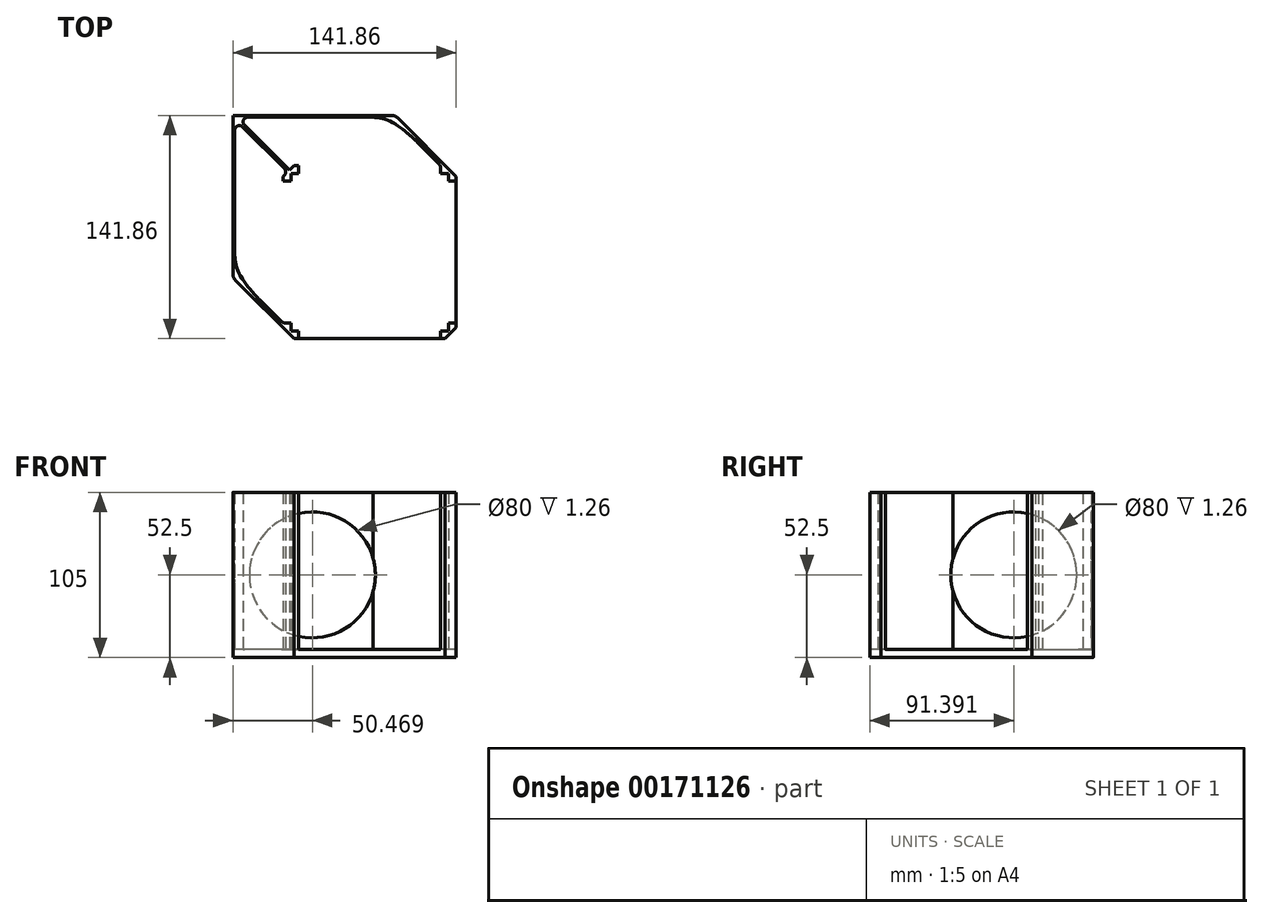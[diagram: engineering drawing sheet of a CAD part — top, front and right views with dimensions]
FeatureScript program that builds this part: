
annotation { "Feature Type Name" : "Feature", "Feature Type Description" : "" }
export const myFeature = defineFeature(function(context is Context, id is Id, definition is map)
    precondition{}
    {
        {
            var Q0;
            Q0=qCreatedBy(makeId("Top.planeOp"),FACE);
            var sketch = newSketch(context, id + "F0", { "sketchPlane" : qUnion([Q0])});
            skLineSegment(sketch, "E0.bottom", {"start": v(55, 55) * mm, "end": v(-55, 55) * mm});
            skLineSegment(sketch, "E0.top", {"start": v(55, -55) * mm, "end": v(-55, -55) * mm});
            skLineSegment(sketch, "E0.left", {"start": v(55, 55) * mm, "end": v(55, -55) * mm});
            skLineSegment(sketch, "E0.right", {"start": v(-55, 55) * mm, "end": v(-55, -55) * mm});
            skPoint(sketch, "E0.middle", {"position": v(0, 0) * mm});
            skSolve(sketch);
        }
        {
            var Q0;
            Q0 = qSketchRegion(id + "F0", true);
            extrude(context, id + "F1", {"entities" : qUnion([Q0]), "depth" : 5 * mm});
        }
        {
            var Q0;
            Q0=makeQuery(id+"F1.opExtrude","CAP_FACE",FACE,{"disambiguationData":[OSD([sQuery(id+"F0.wireOp",EDGE,"E0.bottom"),sQuery(id+"F0.wireOp",EDGE,"E0.top"),sQuery(id+"F0.wireOp",EDGE,"E0.left"),sQuery(id+"F0.wireOp",EDGE,"E0.right")])],"isStart":false});
            var sketch = newSketch(context, id + "F2", { "sketchPlane" : qUnion([Q0])});
            skLineSegment(sketch, "E1", {"start": v(-55, -55) * mm, "end": v(-55, -45) * mm});
            skLineSegment(sketch, "E2", {"start": v(-55, -45) * mm, "end": v(-50, -45) * mm});
            skLineSegment(sketch, "E3", {"start": v(-50, -45) * mm, "end": v(-50, -50) * mm});
            skLineSegment(sketch, "E4", {"start": v(-50, -50) * mm, "end": v(-45, -50) * mm});
            skLineSegment(sketch, "E5", {"start": v(-45, -50) * mm, "end": v(-45, -55) * mm});
            skLineSegment(sketch, "E6", {"start": v(-45, -55) * mm, "end": v(-55, -55) * mm});
            skLineSegment(sketch, "E7.MirrorCS", {"start": v(45, -55) * mm, "end": v(55, -55) * mm});
            skLineSegment(sketch, "E8.MirrorCS", {"start": v(45, -50) * mm, "end": v(45, -55) * mm});
            skLineSegment(sketch, "E9.MirrorCS", {"start": v(50, -50) * mm, "end": v(45, -50) * mm});
            skLineSegment(sketch, "E10.MirrorCS", {"start": v(50, -45) * mm, "end": v(50, -50) * mm});
            skLineSegment(sketch, "E11.MirrorCS", {"start": v(55, -55) * mm, "end": v(55, -45) * mm});
            skLineSegment(sketch, "E12.MirrorCS", {"start": v(55, -45) * mm, "end": v(50, -45) * mm});
            skLineSegment(sketch, "E13.MirrorCS", {"start": v(55, 45) * mm, "end": v(50, 45) * mm});
            skLineSegment(sketch, "E14.MirrorCS", {"start": v(-50, 45) * mm, "end": v(-50, 50) * mm});
            skLineSegment(sketch, "E15.MirrorCS", {"start": v(50, 50) * mm, "end": v(45, 50) * mm});
            skLineSegment(sketch, "E16.MirrorCS", {"start": v(50, 45) * mm, "end": v(50, 50) * mm});
            skLineSegment(sketch, "E17.MirrorCS", {"start": v(-50, 50) * mm, "end": v(-45, 50) * mm});
            skLineSegment(sketch, "E18.MirrorCS", {"start": v(-45, 50) * mm, "end": v(-45, 55) * mm});
            skLineSegment(sketch, "E19.MirrorCS", {"start": v(45, 50) * mm, "end": v(45, 55) * mm});
            skLineSegment(sketch, "E20.MirrorCS", {"start": v(-55, 45) * mm, "end": v(-50, 45) * mm});
            skLineSegment(sketch, "E21.MirrorCS", {"start": v(-45, 55) * mm, "end": v(-55, 55) * mm});
            skLineSegment(sketch, "E22.MirrorCS", {"start": v(55, 55) * mm, "end": v(55, 45) * mm});
            skLineSegment(sketch, "E23.MirrorCS", {"start": v(-55, 55) * mm, "end": v(-55, 45) * mm});
            skLineSegment(sketch, "E24.MirrorCS", {"start": v(45, 55) * mm, "end": v(55, 55) * mm});
            skSolve(sketch);
        }
        {
            var Q0;
            Q0 = qSketchRegion(id + "F2", true);
            extrude(context, id + "F3", {"entities" : qUnion([Q0]), "operationType" : NewBodyOperationType.ADD, "depth" : 100 * mm});
        }
        {
            var Q0;
            Q0=makeQuery(id+"F3.boolean.opBoolean","MERGE",EDGE,{"derivedFrom":[makeQuery(id+"F1.opExtrude","SWEPT_EDGE",EDGE,{"disambiguationData":[OSD([sQuery(id+"F0.wireOp",EDGE,"E0.top"),sQuery(id+"F0.wireOp",EDGE,"E0.left")])]}),makeQuery(id+"F3.opExtrude","SWEPT_EDGE",EDGE,{"disambiguationData":[OSD([sQuery(id+"F2.wireOp",EDGE,"E7.MirrorCS"),sQuery(id+"F2.wireOp",EDGE,"E11.MirrorCS")])]})]});
            var Q1;
            Q1=makeQuery(id+"F3.boolean.opBoolean","MERGE",EDGE,{"derivedFrom":[makeQuery(id+"F1.opExtrude","SWEPT_EDGE",EDGE,{"disambiguationData":[OSD([sQuery(id+"F0.wireOp",EDGE,"E0.bottom"),sQuery(id+"F0.wireOp",EDGE,"E0.left")])]}),makeQuery(id+"F3.opExtrude","SWEPT_EDGE",EDGE,{"disambiguationData":[OSD([sQuery(id+"F2.wireOp",EDGE,"E22.MirrorCS"),sQuery(id+"F2.wireOp",EDGE,"E24.MirrorCS")])]})]});
            var Q2;
            Q2=makeQuery(id+"F3.boolean.opBoolean","MERGE",EDGE,{"derivedFrom":[makeQuery(id+"F1.opExtrude","SWEPT_EDGE",EDGE,{"disambiguationData":[OSD([sQuery(id+"F0.wireOp",EDGE,"E0.top"),sQuery(id+"F0.wireOp",EDGE,"E0.right")])]}),makeQuery(id+"F3.opExtrude","SWEPT_EDGE",EDGE,{"disambiguationData":[OSD([sQuery(id+"F2.wireOp",EDGE,"E6"),sQuery(id+"F2.wireOp",EDGE,"E1")])]})]});
            var Q3;
            Q3=makeQuery(id+"F3.boolean.opBoolean","MERGE",EDGE,{"derivedFrom":[makeQuery(id+"F1.opExtrude","SWEPT_EDGE",EDGE,{"disambiguationData":[OSD([sQuery(id+"F0.wireOp",EDGE,"E0.bottom"),sQuery(id+"F0.wireOp",EDGE,"E0.right")])]}),makeQuery(id+"F3.opExtrude","SWEPT_EDGE",EDGE,{"disambiguationData":[OSD([sQuery(id+"F2.wireOp",EDGE,"E23.MirrorCS"),sQuery(id+"F2.wireOp",EDGE,"E21.MirrorCS")])]})]});
            chamfer(context, id + "F4", {"entities" : qUnion([Q0, Q1, Q2, Q3]), "width" : 7 * mm, "tangentPropagation" : true});
        }
        {
            var Q0;
            Q0=makeQuery(id+"F1.opExtrude","CAP_FACE",FACE,{"disambiguationData":[OSD([sQuery(id+"F0.wireOp",EDGE,"E0.bottom"),sQuery(id+"F0.wireOp",EDGE,"E0.top"),sQuery(id+"F0.wireOp",EDGE,"E0.left"),sQuery(id+"F0.wireOp",EDGE,"E0.right")])],"isStart":true});
            var sketch = newSketch(context, id + "F5", { "sketchPlane" : qUnion([Q0])});
            skLineSegment(sketch, "E25", {"start": v(-55, 48) * mm, "end": v(-86.86, 16.14) * mm});
            skLineSegment(sketch, "E26", {"start": v(-86.86, 16.14) * mm, "end": v(-86.86, -86.86) * mm});
            skLineSegment(sketch, "E27.MirrorCS", {"start": v(16.14, -86.86) * mm, "end": v(-86.86, -86.86) * mm});
            skLineSegment(sketch, "E28.MirrorCS", {"start": v(48, -55) * mm, "end": v(16.14, -86.86) * mm});
            skSolve(sketch);
        }
        {
            var Q0;
            Q0=makeQuery(id+"F5.imprint","IMPRINT",FACE,{"disambiguationData":[TD([[makeQuery(id+"F5.imprint","IMPRINT",EDGE,{"derivedFrom":sQuery(id+"F5.wireOp",EDGE,"E25")}),1.0]])]});
            extrude(context, id + "F6", {"entities" : qUnion([Q0]), "operationType" : NewBodyOperationType.ADD, "oppositeDirection" : true, "depth" : 5 * mm});
        }
        {
            var Q0;
            {var subQ0=sQuery(id+"F0.wireOp",EDGE,"E0.right");var subQ1=sQuery(id+"F0.wireOp",EDGE,"E0.left");var subQ2=sQuery(id+"F0.wireOp",EDGE,"E0.top");var subQ3=sQuery(id+"F0.wireOp",EDGE,"E0.bottom");Q0=makeQuery(id+"F6.boolean.opBoolean","MERGE",FACE,{"derivedFrom":[makeQuery(id+"F1.opExtrude","CAP_FACE",FACE,{"disambiguationData":[OSD([subQ3,subQ2,subQ1,subQ0])],"isStart":false}),makeQuery(id+"F6.opExtrude","CAP_FACE",FACE,{"disambiguationData":[OSD([subQ3,subQ2,subQ1,subQ0,sQuery(id+"F2.wireOp",EDGE,"E23.MirrorCS"),sQuery(id+"F2.wireOp",EDGE,"E21.MirrorCS"),sQuery(id+"F5.wireOp",EDGE,"E25"),sQuery(id+"F5.wireOp",EDGE,"E26"),sQuery(id+"F5.wireOp",EDGE,"E27.MirrorCS"),sQuery(id+"F5.wireOp",EDGE,"E28.MirrorCS")])],"isStart":false})]});}
            var sketch = newSketch(context, id + "F7", { "sketchPlane" : qUnion([Q0])});
            skLineSegment(sketch, "E29", {"start": v(-55, -48) * mm, "end": v(-86.86, -16.14) * mm});
            skLineSegment(sketch, "E30", {"start": v(-86.86, -16.14) * mm, "end": v(-86.86, 86.86) * mm});
            skLineSegment(sketch, "E31", {"start": v(-50, 50) * mm, "end": v(-50.53, 49.47) * mm});
            skLineSegment(sketch, "E32", {"start": v(-50.53, 49.47) * mm, "end": v(-85.69, 84.63) * mm});
            skLineSegment(sketch, "E33", {"start": v(-85.69, -2.59) * mm, "end": v(-85.69, 84.63) * mm});
            skFitSpline(sketch, "E34", {"points": [v(-55, -45) * mm, v(-73.9, -25.88) * mm, v(-83.72, -11.72) * mm, v(-85.69, -2.27) * mm], "startDerivative": vector(-48.1, 46.47) * mm, "endDerivative": vector(-2.15, 37.07) * mm});
            skLineSegment(sketch, "E35.MirrorCS", {"start": v(-49.47, 50.53) * mm, "end": v(-84.63, 85.69) * mm});
            skLineSegment(sketch, "E36.MirrorCS", {"start": v(2.59, 85.69) * mm, "end": v(-84.63, 85.69) * mm});
            skLineSegment(sketch, "E37.MirrorCS", {"start": v(16.14, 86.86) * mm, "end": v(-86.86, 86.86) * mm});
            skLineSegment(sketch, "E38.MirrorCS", {"start": v(-50, 50) * mm, "end": v(-49.47, 50.53) * mm});
            skFitSpline(sketch, "E39.MirrorCS", {"points": [v(45, 55) * mm, v(25.88, 73.9) * mm, v(11.72, 83.72) * mm, v(2.27, 85.69) * mm], "startDerivative": vector(-46.47, 48.1) * mm, "endDerivative": vector(-37.07, 2.15) * mm});
            skLineSegment(sketch, "E40.MirrorCS", {"start": v(48, 55) * mm, "end": v(16.14, 86.86) * mm});
            skLineSegment(sketch, "E41", {"start": v(-55, -48) * mm, "end": v(-55, -45) * mm});
            skLineSegment(sketch, "E42", {"start": v(45, 55) * mm, "end": v(48, 55) * mm});
            skSolve(sketch);
        }
        {
            var Q0;
            Q0=makeQuery(id+"F7.imprint","IMPRINT",FACE,{"disambiguationData":[TD([[makeQuery(id+"F7.imprint","IMPRINT",EDGE,{"derivedFrom":sQuery(id+"F7.wireOp",EDGE,"E29")}),-1.0]])]});
            extrude(context, id + "F8", {"entities" : qUnion([Q0]), "operationType" : NewBodyOperationType.ADD, "depth" : 100 * mm});
        }
        {
            var Q0;
            Q0=makeQuery(id+"F8.opExtrude","SWEPT_EDGE",EDGE,{"disambiguationData":[OSD([sQuery(id+"F0.wireOp",EDGE,"E0.bottom"),sQuery(id+"F0.wireOp",EDGE,"E0.top"),sQuery(id+"F0.wireOp",EDGE,"E0.left"),sQuery(id+"F0.wireOp",EDGE,"E0.right"),sQuery(id+"F2.wireOp",EDGE,"E23.MirrorCS"),sQuery(id+"F2.wireOp",EDGE,"E21.MirrorCS"),sQuery(id+"F7.wireOp",EDGE,"E35.MirrorCS")])]});
            var Q1;
            Q1=makeQuery(id+"F8.opExtrude","SWEPT_EDGE",EDGE,{"disambiguationData":[OSD([sQuery(id+"F0.wireOp",EDGE,"E0.bottom"),sQuery(id+"F0.wireOp",EDGE,"E0.top"),sQuery(id+"F0.wireOp",EDGE,"E0.left"),sQuery(id+"F0.wireOp",EDGE,"E0.right"),sQuery(id+"F2.wireOp",EDGE,"E23.MirrorCS"),sQuery(id+"F2.wireOp",EDGE,"E21.MirrorCS"),sQuery(id+"F7.wireOp",EDGE,"E32")])]});
            fillet(context, id + "F9", {"entities" : qUnion([Q0, Q1]), "radius" : 3 * mm, "tangentPropagation" : true, "allowEdgeOverflow" : false});
        }
        {
            var Q0;
            {var subQ0=sQuery(id+"F2.wireOp",EDGE,"E19.MirrorCS");Q0=makeQuery(id+"F8.boolean.opBoolean","MERGE",EDGE,{"derivedFrom":[makeQuery(id+"F3.opExtrude","SWEPT_EDGE",EDGE,{"disambiguationData":[OSD([sQuery(id+"F0.wireOp",EDGE,"E0.bottom"),subQ0,sQuery(id+"F2.wireOp",EDGE,"E24.MirrorCS")])]}),makeQuery(id+"F8.opExtrude","SWEPT_EDGE",EDGE,{"disambiguationData":[OSD([subQ0,sQuery(id+"F7.wireOp",EDGE,"E39.MirrorCS"),sQuery(id+"F7.wireOp",EDGE,"E42")])]})]});}
            var Q1;
            {var subQ0=sQuery(id+"F2.wireOp",EDGE,"E2");Q1=makeQuery(id+"F8.boolean.opBoolean","MERGE",EDGE,{"derivedFrom":[makeQuery(id+"F3.opExtrude","SWEPT_EDGE",EDGE,{"disambiguationData":[OSD([sQuery(id+"F0.wireOp",EDGE,"E0.right"),subQ0,sQuery(id+"F2.wireOp",EDGE,"E1")])]}),makeQuery(id+"F8.opExtrude","SWEPT_EDGE",EDGE,{"disambiguationData":[OSD([subQ0,sQuery(id+"F7.wireOp",EDGE,"E34"),sQuery(id+"F7.wireOp",EDGE,"E41")])]})]});}
            var Q2;
            Q2=makeQuery(id+"F8.opExtrude","SWEPT_EDGE",EDGE,{"disambiguationData":[OSD([sQuery(id+"F7.wireOp",EDGE,"E32"),sQuery(id+"F7.wireOp",EDGE,"E33")])]});
            var Q3;
            Q3=makeQuery(id+"F8.opExtrude","SWEPT_EDGE",EDGE,{"disambiguationData":[OSD([sQuery(id+"F7.wireOp",EDGE,"E35.MirrorCS"),sQuery(id+"F7.wireOp",EDGE,"E36.MirrorCS")])]});
            fillet(context, id + "F10", {"entities" : qUnion([Q0, Q1, Q2, Q3]), "radius" : 3 * mm, "tangentPropagation" : true, "allowEdgeOverflow" : false});
        }
        {
            var Q0;
            Q0=makeQuery(id+"F8.boolean.opBoolean","MERGE",EDGE,{"derivedFrom":[makeQuery(id+"F6.opExtrude","SWEPT_EDGE",EDGE,{"disambiguationData":[OSD([sQuery(id+"F5.wireOp",EDGE,"E25"),sQuery(id+"F5.wireOp",EDGE,"E26")])]}),makeQuery(id+"F8.opExtrude","SWEPT_EDGE",EDGE,{"disambiguationData":[OSD([sQuery(id+"F7.wireOp",EDGE,"E29"),sQuery(id+"F7.wireOp",EDGE,"E30")])]})]});
            var Q1;
            Q1=makeQuery(id+"F8.boolean.opBoolean","MERGE",EDGE,{"derivedFrom":[makeQuery(id+"F6.opExtrude","SWEPT_EDGE",EDGE,{"disambiguationData":[OSD([sQuery(id+"F5.wireOp",EDGE,"E27.MirrorCS"),sQuery(id+"F5.wireOp",EDGE,"E28.MirrorCS")])]}),makeQuery(id+"F8.opExtrude","SWEPT_EDGE",EDGE,{"disambiguationData":[OSD([sQuery(id+"F7.wireOp",EDGE,"E37.MirrorCS"),sQuery(id+"F7.wireOp",EDGE,"E40.MirrorCS")])]})]});
            fillet(context, id + "F11", {"entities" : qUnion([Q0, Q1]), "radius" : 5 * mm, "tangentPropagation" : true, "allowEdgeOverflow" : false});
        }
        {
            var Q0;
            Q0=makeQuery(id+"F8.boolean.opBoolean","MERGE",FACE,{"derivedFrom":[makeQuery(id+"F6.opExtrude","SWEPT_FACE",FACE,{"disambiguationData":[OSD([sQuery(id+"F5.wireOp",EDGE,"E27.MirrorCS")])]}),makeQuery(id+"F8.opExtrude","SWEPT_FACE",FACE,{"disambiguationData":[OSD([sQuery(id+"F7.wireOp",EDGE,"E37.MirrorCS")])]})]});
            var sketch = newSketch(context, id + "F12", { "sketchPlane" : qUnion([Q0])});
            skCircle(sketch, "E43", {"center": v(36.4, 52.5) * mm, "radius": 40 * mm});
            skSolve(sketch);
        }
        {
            var Q0;
            Q0=makeQuery(id+"F12.imprint","IMPRINT",FACE,{"disambiguationData":[TD([[makeQuery(id+"F12.imprint","IMPRINT",EDGE,{"derivedFrom":sQuery(id+"F12.wireOp",EDGE,"E43")}),1.0]])]});
            extrude(context, id + "F13", {"entities" : qUnion([Q0]), "operationType" : NewBodyOperationType.REMOVE, "oppositeDirection" : true, "depth" : 2 * mm});
        }
        {
            var Q0;
            Q0=makeQuery(id+"F8.boolean.opBoolean","MERGE",FACE,{"derivedFrom":[makeQuery(id+"F6.opExtrude","SWEPT_FACE",FACE,{"disambiguationData":[OSD([sQuery(id+"F5.wireOp",EDGE,"E26")])]}),makeQuery(id+"F8.opExtrude","SWEPT_FACE",FACE,{"disambiguationData":[OSD([sQuery(id+"F7.wireOp",EDGE,"E30")])]})]});
            var sketch = newSketch(context, id + "F14", { "sketchPlane" : qUnion([Q0])});
            skCircle(sketch, "E44", {"center": v(-36.4, 52.5) * mm, "radius": 40 * mm});
            skSolve(sketch);
        }
        {
            var Q0;
            Q0 = qSketchRegion(id + "F14", true);
            extrude(context, id + "F15", {"entities" : qUnion([Q0]), "operationType" : NewBodyOperationType.REMOVE, "oppositeDirection" : true, "depth" : 2 * mm});
        }
    });
